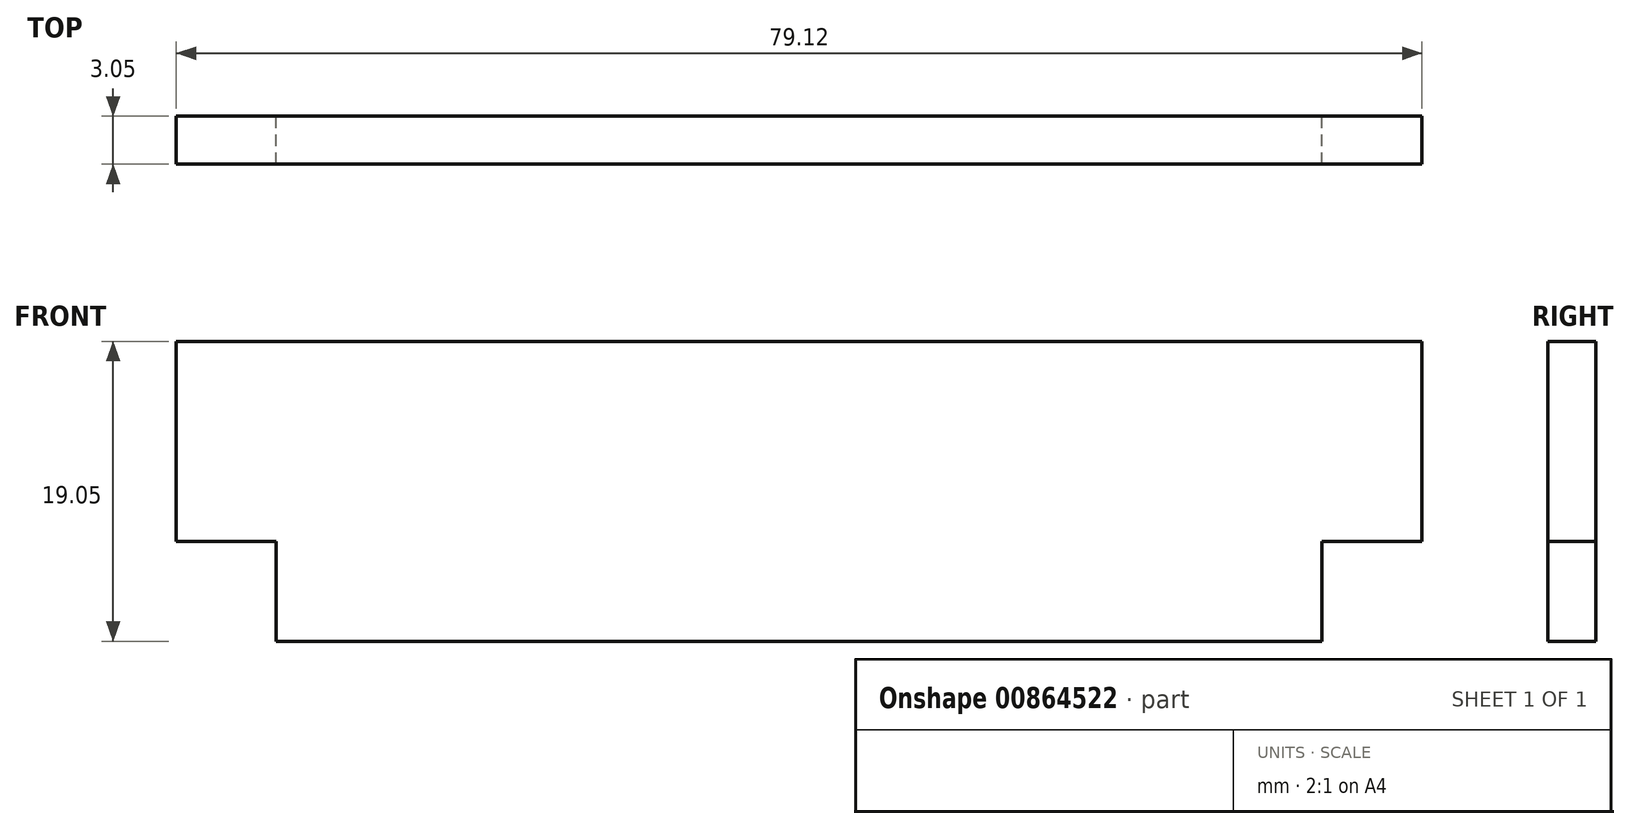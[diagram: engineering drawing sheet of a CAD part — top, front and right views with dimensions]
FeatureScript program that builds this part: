
annotation { "Feature Type Name" : "Feature", "Feature Type Description" : "" }
export const myFeature = defineFeature(function(context is Context, id is Id, definition is map)
    precondition{}
    {
        {
            var Q0;
            Q0=qCreatedBy(makeId("Front.planeOp"),FACE);
            var sketch = newSketch(context, id + "F0", { "sketchPlane" : qUnion([Q0])});
            skLineSegment(sketch, "E0", {"start": v(-39.56, 0) * mm, "end": v(-39.56, 12.7) * mm});
            skLineSegment(sketch, "E1", {"start": v(-39.56, 12.7) * mm, "end": v(39.56, 12.7) * mm});
            skLineSegment(sketch, "E2", {"start": v(39.56, 12.7) * mm, "end": v(39.56, 0) * mm});
            skLineSegment(sketch, "E3", {"start": v(39.56, 0) * mm, "end": v(33.2, 0) * mm});
            skLineSegment(sketch, "E4", {"start": v(33.2, 0) * mm, "end": v(33.2, -6.35) * mm});
            skLineSegment(sketch, "E5", {"start": v(33.2, -6.35) * mm, "end": v(-33.2, -6.35) * mm});
            skLineSegment(sketch, "E6", {"start": v(-33.2, -6.35) * mm, "end": v(-33.2, 0) * mm});
            skLineSegment(sketch, "E7", {"start": v(-33.2, 0) * mm, "end": v(-39.56, 0) * mm});
            skSolve(sketch);
        }
        {
            var Q0;
            Q0 = qSketchRegion(id + "F0", true);
            extrude(context, id + "F1", {"entities" : qUnion([Q0]), "depth" : 3.05 * mm, "offsetDistance" : 25.4 * mm});
        }
    });
